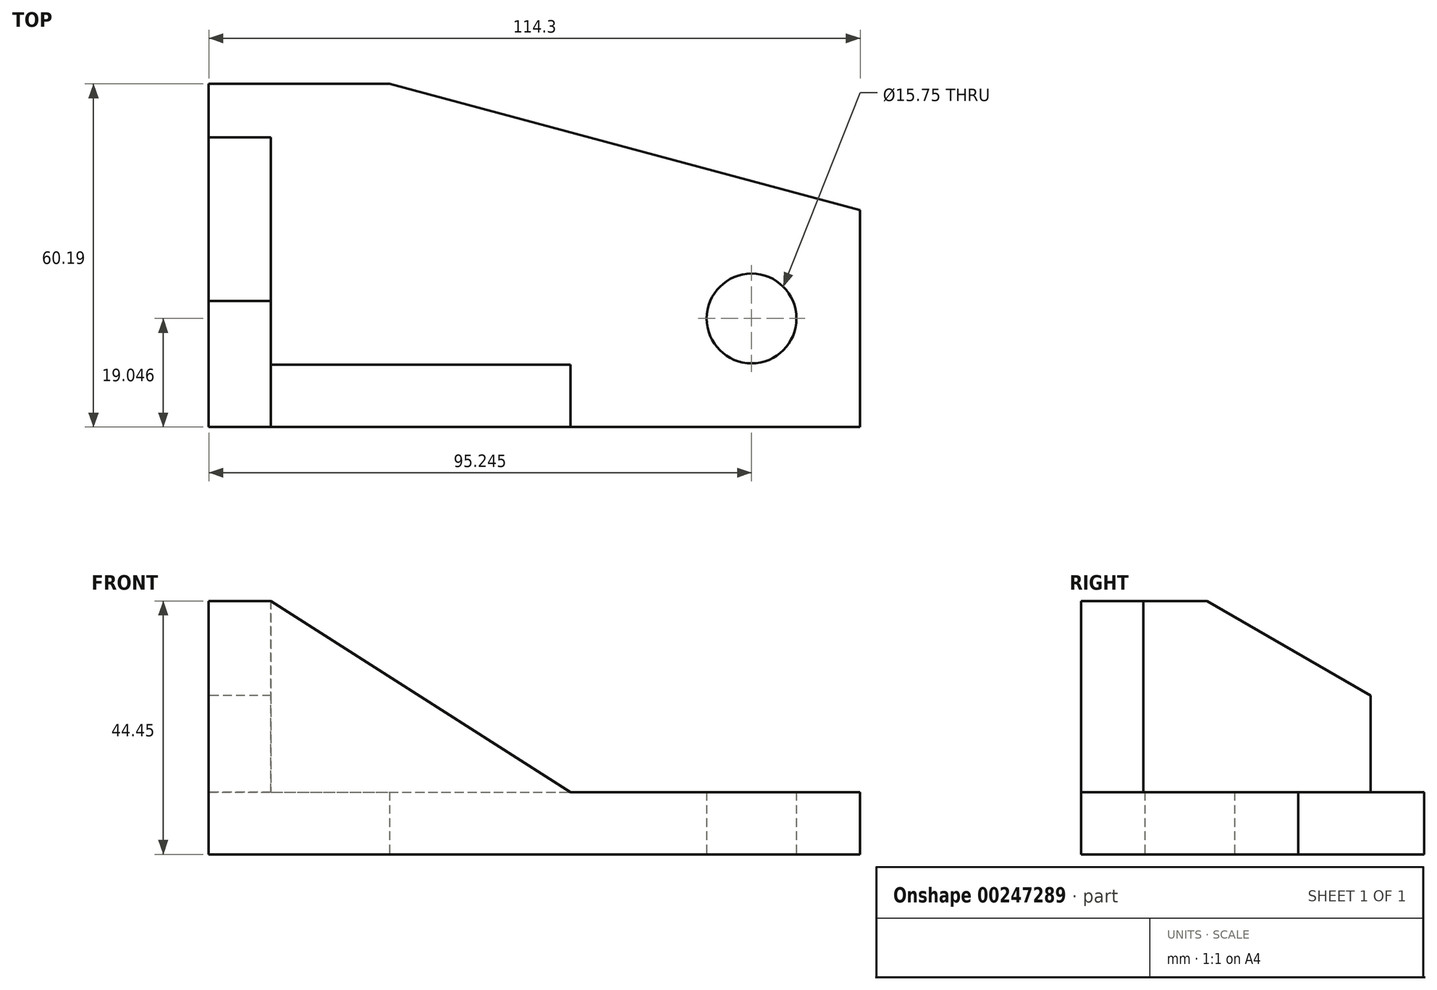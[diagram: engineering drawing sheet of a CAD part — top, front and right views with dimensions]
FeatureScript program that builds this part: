
annotation { "Feature Type Name" : "Feature", "Feature Type Description" : "" }
export const myFeature = defineFeature(function(context is Context, id is Id, definition is map)
    precondition{}
    {
        {
            var Q0;
            Q0=qCreatedBy(makeId("Top.planeOp"),FACE);
            var sketch = newSketch(context, id + "F0", { "sketchPlane" : qUnion([Q0])});
            skLineSegment(sketch, "E0", {"start": v(-47.66, -40.97) * mm, "end": v(66.64, -40.97) * mm});
            skLineSegment(sketch, "E1", {"start": v(-47.66, -40.97) * mm, "end": v(-47.66, 19.22) * mm});
            skLineSegment(sketch, "E2", {"start": v(-47.66, 19.22) * mm, "end": v(-15.91, 19.22) * mm});
            skLineSegment(sketch, "E3", {"start": v(-15.91, 19.22) * mm, "end": v(73.3, 19.22) * mm, "construction": true});
            skLineSegment(sketch, "E4", {"start": v(-15.91, 19.22) * mm, "end": v(66.64, -2.9) * mm});
            skLineSegment(sketch, "E5", {"start": v(66.64, -40.97) * mm, "end": v(66.64, -2.9) * mm});
            skCircle(sketch, "E6", {"center": v(47.59, -21.92) * mm, "radius": 7.87 * mm});
            skSolve(sketch);
        }
        {
            var Q0;
            Q0 = qSketchRegion(id + "F0", true);
            extrude(context, id + "F1", {"entities" : qUnion([Q0]), "depth" : 10.92 * mm});
        }
        {
            var Q0;
            Q0=makeQuery(id+"F1.opExtrude","SWEPT_FACE",FACE,{"disambiguationData":[OSD([sQuery(id+"F0.wireOp",EDGE,"E1")])]});
            var sketch = newSketch(context, id + "F2", { "sketchPlane" : qUnion([Q0])});
            skLineSegment(sketch, "E7", {"start": v(40.97, 10.92) * mm, "end": v(40.97, 44.45) * mm});
            skLineSegment(sketch, "E8", {"start": v(40.97, 44.45) * mm, "end": v(18.88, 44.45) * mm});
            skLineSegment(sketch, "E9", {"start": v(18.88, 44.45) * mm, "end": v(-22.65, 44.45) * mm, "construction": true});
            skLineSegment(sketch, "E10", {"start": v(18.88, 44.45) * mm, "end": v(-9.83, 27.88) * mm});
            skLineSegment(sketch, "E11", {"start": v(-9.83, 27.88) * mm, "end": v(-9.83, 10.92) * mm});
            skSolve(sketch);
        }
        {
            var Q0;
            {var subQ1=sQuery(id+"F2.wireOp",EDGE,"E7");Q0=makeQuery(id+"F2.imprint","IMPRINT",FACE,{"disambiguationData":[TD([[makeQuery(id+"F2.imprint","IMPRINT",EDGE,{"derivedFrom":subQ1}),1.0]])]});}
            extrude(context, id + "F3", {"entities" : qUnion([Q0]), "oppositeDirection" : true, "depth" : 10.92 * mm});
        }
        {
            var Q0;
            Q0=makeQuery(id+"F3.opExtrude","SWEPT_FACE",FACE,{"disambiguationData":[OSD([sQuery(id+"F2.wireOp",EDGE,"E7")])]});
            var sketch = newSketch(context, id + "F4", { "sketchPlane" : qUnion([Q0])});
            skLineSegment(sketch, "E12", {"start": v(-36.74, 44.45) * mm, "end": v(15.84, 10.92) * mm});
            skLineSegment(sketch, "E13", {"start": v(-36.74, 44.45) * mm, "end": v(-36.74, 10.92) * mm});
            skLineSegment(sketch, "E14", {"start": v(-36.74, 10.92) * mm, "end": v(15.84, 10.92) * mm});
            skSolve(sketch);
        }
        {
            var Q0;
            Q0 = qSketchRegion(id + "F4", true);
            extrude(context, id + "F5", {"entities" : qUnion([Q0]), "operationType" : NewBodyOperationType.ADD, "oppositeDirection" : true, "depth" : 10.92 * mm});
        }
    });
